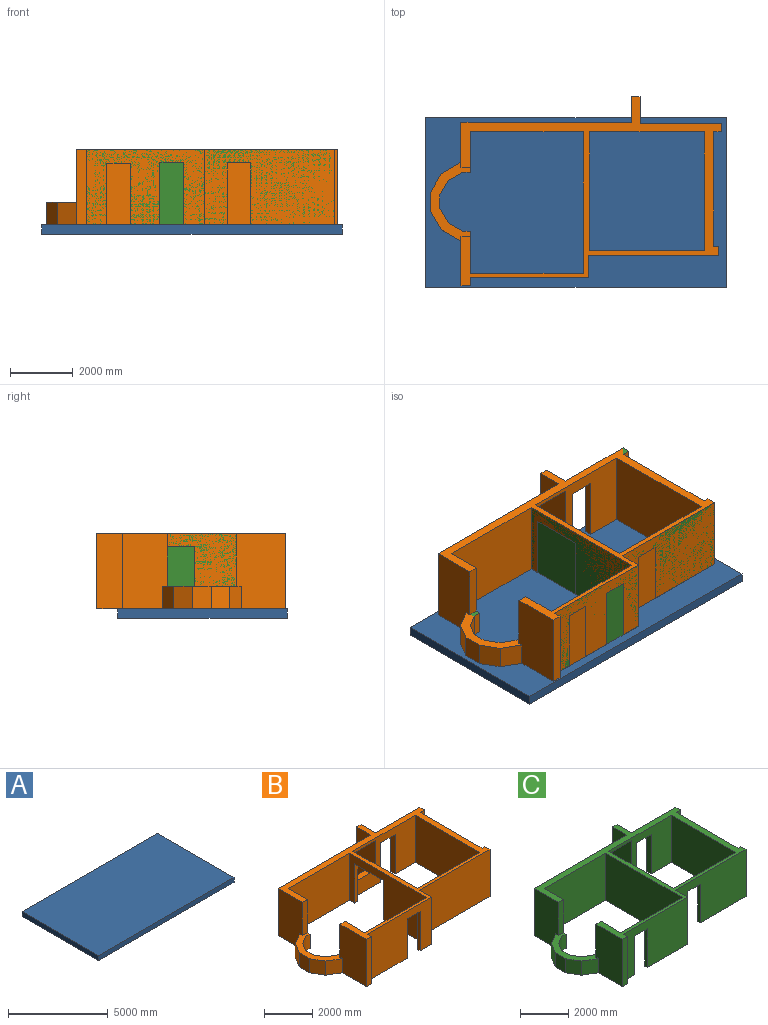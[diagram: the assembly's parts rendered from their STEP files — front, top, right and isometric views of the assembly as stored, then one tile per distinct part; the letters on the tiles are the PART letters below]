
ASSEMBLY  parts=3 mates=1
PART A: 6 faces, bbox 9590x5410x300 mm
  f0: plane 9590x300mm, normal (0,1,0), area 2877000mm2, adj f1,f3,f4,f5
  f1: plane 5410x300mm, normal (-1,0,0), area 1623000mm2, adj f0,f2,f4,f5
  f2: plane 9590x300mm, normal (0,-1,0), area 2877000mm2, adj f1,f3,f4,f5
  f3: plane 5410x300mm, normal (1,0,0), area 1623000mm2, adj f0,f2,f4,f5
  f4: plane 9590x5410mm, normal (0,0,-1), area 51881900mm2, adj f0,f1,f2,f3
  f5: plane 9590x5410mm, normal (0,0,1), area 51881900mm2, adj f0,f1,f2,f3
PART B: 56 faces, bbox 9290x6030x2400 mm
  f0: plane 4520x2400mm, normal (-1,0,0), area 7448000mm2, adj f2,f4,f24,f29,f30,f53,f54,f55
  f1: plane 3800x2400mm, normal (1,0,0), area 5720000mm2, adj f2,f6,f27,f29,f30,f53,f54,f55
  f2: plane 4920x4910mm, normal (0,0,-1), area 2774900mm2, adj f0,f1,f3,f4,f5,f6,f10,f11
  f3: plane 3780x2400mm, normal (0,-1,0), area 7552000mm2, adj f2,f9,f10,f29,f30,f50,f51,f52
  f4: plane 3610x2400mm, normal (0,1,0), area 7144000mm2, adj f0,f2,f25,f29,f30,f50,f51,f52
  f5: plane 2600x2400mm, normal (0,1,0), area 4560000mm2, adj f2,f16,f17,f29,f30,f44,f45,f46
  f6: plane 3670x2400mm, normal (0,-1,0), area 5304100mm2, adj f1,f2,f19,f26,f29,f30,f44,f45
  f7: plane 2400x1560mm, normal (-1,0,0), area 3644969.3mm2, adj f8,f28,f29,f30,f31,f43
  f8: plane 2400x300mm, normal (0,-1,0), area 720000mm2, adj f7,f9,f29,f30
  f9: plane 2400x250mm, normal (1,0,0), area 600000mm2, adj f3,f8,f29,f30
  f10: plane 2400x710mm, normal (1,0,0), area 1704000mm2, adj f2,f3,f11,f29
  f11: plane 4160x2400mm, normal (0,-1,0), area 9984000mm2, adj f2,f10,f12,f29
  f12: plane 2400x300mm, normal (1,0,0), area 720000mm2, adj f2,f11,f13,f29
  f13: plane 2400x170mm, normal (0,1,0), area 408000mm2, adj f2,f12,f14,f29
  f14: plane 3650x2400mm, normal (1,0,0), area 8760000mm2, adj f2,f13,f15,f29
  f15: plane 2400x250mm, normal (0,-1,0), area 600000mm2, adj f2,f14,f16,f29
  f16: plane 2400x260mm, normal (1,0,0), area 624000mm2, adj f2,f5,f15,f29
  f17: plane 2400x860mm, normal (1,0,0), area 2064000mm2, adj f5,f18,f29,f30
  f18: plane 2400x260mm, normal (0,1,0), area 624000mm2, adj f17,f19,f29,f30
  f19: plane 2400x1120mm, normal (-1,0,0), area 2416500mm2, adj f6,f18,f20,f29,f30,f47,f48
  f20: plane 5460x2400mm, normal (0,1,0), area 11280100mm2, adj f19,f21,f29,f30,f47,f48,f49
  f21: plane 2400x1430mm, normal (-1,0,0), area 3318569.3mm2, adj f20,f22,f29,f30,f39,f43
  f22: plane 1680x300mm, normal (0,-1,0), area 504000mm2, adj f21,f23,f29,f43
  f23: plane 2400x1290mm, normal (1,0,0), area 2827200mm2, adj f22,f24,f29,f30,f38,f43
  f24: plane 3610x2400mm, normal (0,-1,0), area 8664000mm2, adj f0,f23,f29,f30
  f25: plane 2400x1350mm, normal (1,0,0), area 2937600mm2, adj f4,f28,f29,f30,f32,f43
  f26: plane 3800x2400mm, normal (-1,0,0), area 9120000mm2, adj f2,f6,f27,f29
  f27: plane 3670x2400mm, normal (0,1,0), area 8808000mm2, adj f1,f2,f26,f29
  f28: plane 1680x300mm, normal (0,1,0), area 504000mm2, adj f7,f25,f29,f43
  f29: plane 8320x6030mm, normal (0,0,1), area 6575300mm2, adj f0,f1,f3,f4,f5,f6,f7,f8
  f30: plane 6730x6030mm, normal (0,0,-1), area 4117317.5mm2, adj f0,f1,f3,f4,f5,f6,f7,f8
  f31: plane 720x626.08mm, normal (-0.5,-0.87,0), area 520510.6mm2, adj f7,f30,f42,f43
  f32: plane 720x250mm, normal (0,1,0), area 180000mm2, adj f25,f30,f33,f43
  f33: plane 720x456.46mm, normal (0.5,0.87,0), area 379495.1mm2, adj f30,f32,f34,f43
  f34: plane 720x456.46mm, normal (0.87,0.5,0), area 379495.1mm2, adj f30,f33,f35,f43
  f35: plane 720x440mm, normal (1,0,0), area 316800mm2, adj f30,f34,f36,f43
  f36: plane 720x456.46mm, normal (0.87,-0.5,0), area 379495.1mm2, adj f30,f35,f37,f43
  f37: plane 720x456.46mm, normal (0.5,-0.87,0), area 379495.1mm2, adj f30,f36,f38,f43
  f38: plane 720x250mm, normal (0,-1,0), area 180000mm2, adj f23,f30,f37,f43
  f39: plane 720x626.08mm, normal (-0.5,0.87,0), area 520510.6mm2, adj f21,f30,f40,f43
  f40: plane 720x595.69mm, normal (-0.87,0.5,0), area 495249.2mm2, adj f30,f39,f41,f43
  f41: plane 720x600.77mm, normal (-1,0,0), area 432554.1mm2, adj f30,f40,f42,f43
  f42: plane 720x595.69mm, normal (-0.87,-0.5,0), area 495249.2mm2, adj f30,f31,f41,f43
  f43: plane 2515.09x1270mm, normal (0,0,1), area 981717.5mm2, adj f7,f21,f22,f23,f25,f28,f31,f32
  f44: plane 2000x260mm, normal (1,0,0), area 520000mm2, adj f5,f6,f30,f46
  f45: plane 2000x260mm, normal (-1,0,0), area 520000mm2, adj f2,f5,f6,f46
  f46: plane 840x260mm, normal (0,0,-1), area 218400mm2, adj f5,f6,f44,f45
  f47: plane 1220x300mm, normal (0,0,1), area 366000mm2, adj f6,f19,f20,f49
  f48: plane 1220x300mm, normal (0,0,-1), area 366000mm2, adj f6,f19,f20,f49
  f49: plane 1495x300mm, normal (1,0,0), area 448500mm2, adj f6,f20,f47,f48
  f50: plane 2000x140mm, normal (1,0,0), area 280000mm2, adj f3,f4,f30,f52
  f51: plane 2000x140mm, normal (-1,0,0), area 280000mm2, adj f2,f3,f4,f52
  f52: plane 760x140mm, normal (0,0,-1), area 106400mm2, adj f3,f4,f50,f51
  f53: plane 2000x200mm, normal (0,-1,0), area 400000mm2, adj f0,f1,f30,f55
  f54: plane 2000x200mm, normal (0,1,0), area 400000mm2, adj f0,f1,f2,f55
  f55: plane 1700x200mm, normal (0,0,-1), area 340000mm2, adj f0,f1,f53,f54
PART C: 56 faces, bbox 9290x6030x2400 mm
  f0: plane 2600x2400mm, normal (0,1,0), area 4560000mm2, adj f2,f15,f16,f29,f30,f50,f51,f52
  f1: plane 3670x2400mm, normal (0,-1,0), area 5304100mm2, adj f2,f18,f26,f27,f29,f30,f50,f51
  f2: plane 4210x2770mm, normal (0,0,-1), area 1978200mm2, adj f0,f1,f4,f6,f11,f12,f13,f14
  f3: plane 3780x2400mm, normal (0,-1,0), area 7594500mm2, adj f9,f10,f29,f30,f47,f48,f49
  f4: plane 4160x2400mm, normal (0,-1,0), area 8518800mm2, adj f2,f10,f11,f29,f30,f44,f45,f46
  f5: plane 3610x2400mm, normal (0,1,0), area 7186500mm2, adj f24,f25,f29,f30,f47,f48,f49
  f6: plane 3670x2400mm, normal (0,1,0), area 7342800mm2, adj f2,f26,f27,f29,f30,f44,f45,f46
  f7: plane 2400x1560mm, normal (-1,0,0), area 3644969.3mm2, adj f8,f28,f29,f30,f31,f43
  f8: plane 2400x300mm, normal (0,-1,0), area 720000mm2, adj f7,f9,f29,f30
  f9: plane 2400x250mm, normal (1,0,0), area 600000mm2, adj f3,f8,f29,f30
  f10: plane 2400x710mm, normal (1,0,0), area 1704000mm2, adj f3,f4,f29,f30
  f11: plane 2400x300mm, normal (1,0,0), area 720000mm2, adj f2,f4,f12,f29
  f12: plane 2400x170mm, normal (0,1,0), area 408000mm2, adj f2,f11,f13,f29
  f13: plane 3650x2400mm, normal (1,0,0), area 8760000mm2, adj f2,f12,f14,f29
  f14: plane 2400x250mm, normal (0,-1,0), area 600000mm2, adj f2,f13,f15,f29
  f15: plane 2400x260mm, normal (1,0,0), area 624000mm2, adj f0,f2,f14,f29
  f16: plane 2400x860mm, normal (1,0,0), area 2064000mm2, adj f0,f17,f29,f30
  f17: plane 2400x260mm, normal (0,1,0), area 624000mm2, adj f16,f18,f29,f30
  f18: plane 2400x1120mm, normal (-1,0,0), area 2416500mm2, adj f1,f17,f19,f29,f30,f53,f54
  f19: plane 5460x2400mm, normal (0,1,0), area 11280100mm2, adj f18,f20,f29,f30,f53,f54,f55
  f20: plane 2400x1430mm, normal (-1,0,0), area 3318569.3mm2, adj f19,f21,f29,f30,f39,f43
  f21: plane 1680x300mm, normal (0,-1,0), area 504000mm2, adj f20,f22,f29,f43
  f22: plane 2400x1290mm, normal (1,0,0), area 2827200mm2, adj f21,f23,f29,f30,f38,f43
  f23: plane 3610x2400mm, normal (0,-1,0), area 8664000mm2, adj f22,f24,f29,f30
  f24: plane 4520x2400mm, normal (-1,0,0), area 10848000mm2, adj f5,f23,f29,f30
  f25: plane 2400x1350mm, normal (1,0,0), area 2937600mm2, adj f5,f28,f29,f30,f32,f43
  f26: plane 3800x2400mm, normal (-1,0,0), area 9120000mm2, adj f1,f2,f6,f29
  f27: plane 3800x2400mm, normal (1,0,0), area 9120000mm2, adj f1,f6,f29,f30
  f28: plane 1680x300mm, normal (0,1,0), area 504000mm2, adj f7,f25,f29,f43
  f29: plane 8320x6030mm, normal (0,0,1), area 6575300mm2, adj f0,f1,f3,f4,f5,f6,f7,f8
  f30: plane 6730x6030mm, normal (0,0,-1), area 5144417.5mm2, adj f0,f1,f3,f4,f5,f6,f7,f8
  f31: plane 720x626.08mm, normal (-0.5,-0.87,0), area 520510.6mm2, adj f7,f30,f42,f43
  f32: plane 720x250mm, normal (0,1,0), area 180000mm2, adj f25,f30,f33,f43
  f33: plane 720x456.46mm, normal (0.5,0.87,0), area 379495.1mm2, adj f30,f32,f34,f43
  f34: plane 720x456.46mm, normal (0.87,0.5,0), area 379495.1mm2, adj f30,f33,f35,f43
  f35: plane 720x440mm, normal (1,0,0), area 316800mm2, adj f30,f34,f36,f43
  f36: plane 720x456.46mm, normal (0.87,-0.5,0), area 379495.1mm2, adj f30,f35,f37,f43
  f37: plane 720x456.46mm, normal (0.5,-0.87,0), area 379495.1mm2, adj f30,f36,f38,f43
  f38: plane 720x250mm, normal (0,-1,0), area 180000mm2, adj f22,f30,f37,f43
  f39: plane 720x626.08mm, normal (-0.5,0.87,0), area 520510.6mm2, adj f20,f30,f40,f43
  f40: plane 720x595.69mm, normal (-0.87,0.5,0), area 495249.2mm2, adj f30,f39,f41,f43
  f41: plane 720x600.77mm, normal (-1,0,0), area 432554.1mm2, adj f30,f40,f42,f43
  f42: plane 720x595.69mm, normal (-0.87,-0.5,0), area 495249.2mm2, adj f30,f31,f41,f43
  f43: plane 2515.09x1270mm, normal (0,0,1), area 981717.5mm2, adj f7,f20,f21,f22,f25,f28,f31,f32
  f44: plane 740x150mm, normal (0,0,-1), area 111000mm2, adj f4,f6,f45,f46
  f45: plane 1980x150mm, normal (1,0,0), area 297000mm2, adj f4,f6,f30,f44
  f46: plane 1980x150mm, normal (-1,0,0), area 297000mm2, adj f2,f4,f6,f44
  f47: plane 1970x140mm, normal (1,0,0), area 275800mm2, adj f3,f5,f30,f49
  f48: plane 1970x140mm, normal (-1,0,0), area 275800mm2, adj f3,f5,f30,f49
  f49: plane 750x140mm, normal (0,0,-1), area 105000mm2, adj f3,f5,f47,f48
  f50: plane 2000x260mm, normal (1,0,0), area 520000mm2, adj f0,f1,f30,f52
  f51: plane 2000x260mm, normal (-1,0,0), area 520000mm2, adj f0,f1,f2,f52
  f52: plane 840x260mm, normal (0,0,-1), area 218400mm2, adj f0,f1,f50,f51
  f53: plane 1220x300mm, normal (0,0,1), area 366000mm2, adj f1,f18,f19,f55
  f54: plane 1220x300mm, normal (0,0,-1), area 366000mm2, adj f1,f18,f19,f55
  f55: plane 1495x300mm, normal (1,0,0), area 448500mm2, adj f1,f19,f53,f54
PLACE A t=(0,0,300)mm
PLACE B t=(0,0,300)mm
PLACE C t=(0,0,300)mm
MATE fastened A.f5 <-> C.f30  axis (0,0,1) through (0,5410,300)mm
